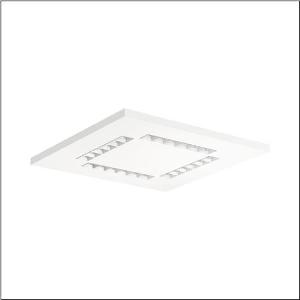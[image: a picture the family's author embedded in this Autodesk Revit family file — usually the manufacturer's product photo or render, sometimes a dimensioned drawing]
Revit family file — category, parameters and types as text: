
# Revit family: silica_r__21_square_51mx6nds44w_aabb
name_source: partatom
category: Lighting Fixtures
units: mm (PartAtom-declared; Revit-internal decimal feet)

## family parameters
Cut with Voids When Loaded = No
Host = Face
Light Source = No
Part Type = Normal
Room Calculation Point = No
Round Connector Dimension = Use Diameter
Shared = No

## types (1)
- --- (1 x LED, 4600 lm, 27 W, 4000K)
    Apparent Load = 27 VA
    CIE Flux Codes = 83 98 100 100 100
    Color Rendering = 80
    Color Temperature = 4000K
    Default Elevation = 1800 mm
    Description = Silica® 21 Square, office luminaire, primary light control with lens, of PMMA, primary anti-glare with reflector, of PC, white, CAT 2 (L<= 3000cd/m²), light emission: direct distribution, primary light characteristic: symmetric, installation type: lay-in mounting, LED, rated luminous flux: 4.600lm, luminous efficacy: 170lm/W, light colour: 840, colour temperature: 4000K, with terminal, 5-pole, mains connection: 220..240V, AC, 50/60Hz, rated input power: 27W, luminaire housing, of aluminium, traffic white (RAL 9016), module: M600, length: 600mm, width: 600mm, height: 32mm, protection rating (complete): IP20, insulation class (complete): insulation class I (protective earthing), certification: CE, permissible operating ambient temperature: 0..+35°C, standard: EN 50419, packaging unit: 1 piece
    Height = 0 mm  [stored 0 ft]
    Lamp = 1 x LED
    Lamp Light Flux = 4600 lm
    Lamp Power = 27 W
    Lamp count = 1
    Length = 597 mm
    Luminous efficacy = 170 lm/W
    Manufacturer = Siteco
    ModVariant = No
    Model = 51MX6NDS44W
    Mounting Place = Ceiling
    Mounting Type = Recessed
    Number of Poles = 1
    OnlyDefault = Yes
    Power Factor = 1
    Product Name = Silica® 21 Square
    Product group = office luminaire | ceiling recessed
    ProductGroupID = 400
    Protection Class = Protection class I
    Protection Degree = IP 20
    RLX_Detail_Level = 1
    RLX_Emergency_Light_Flux = 0 lm
    RLX_Emergency_Type = 0
    RLX_Emergency_Type_DB = No
    RlxData = <blob elided: 37869 chars, md5=93f9c986>
    Socket = socket
    Standby Power = 0 W
    System Light Flux = 4600 lm
    System Power = 27 W
    Type Comments = factory setting: luminous flux: 100 % | dim-lin: 254 | 366 mA
    Type Image = l_1275224.jpg
    URL = http://relux.com
    VarID = @adj_052767
    Voltage = 0 V
    Weight = 0.00 kg
    Width = 597 mm

note: [stored X ft] marks values corroborated as IEEE doubles in the binary element streams (Revit-internal decimal feet)

## geometry (parser evidence)
native form markers: Blend x4, Sweep x10
no freeform markers — native parametric forms only
